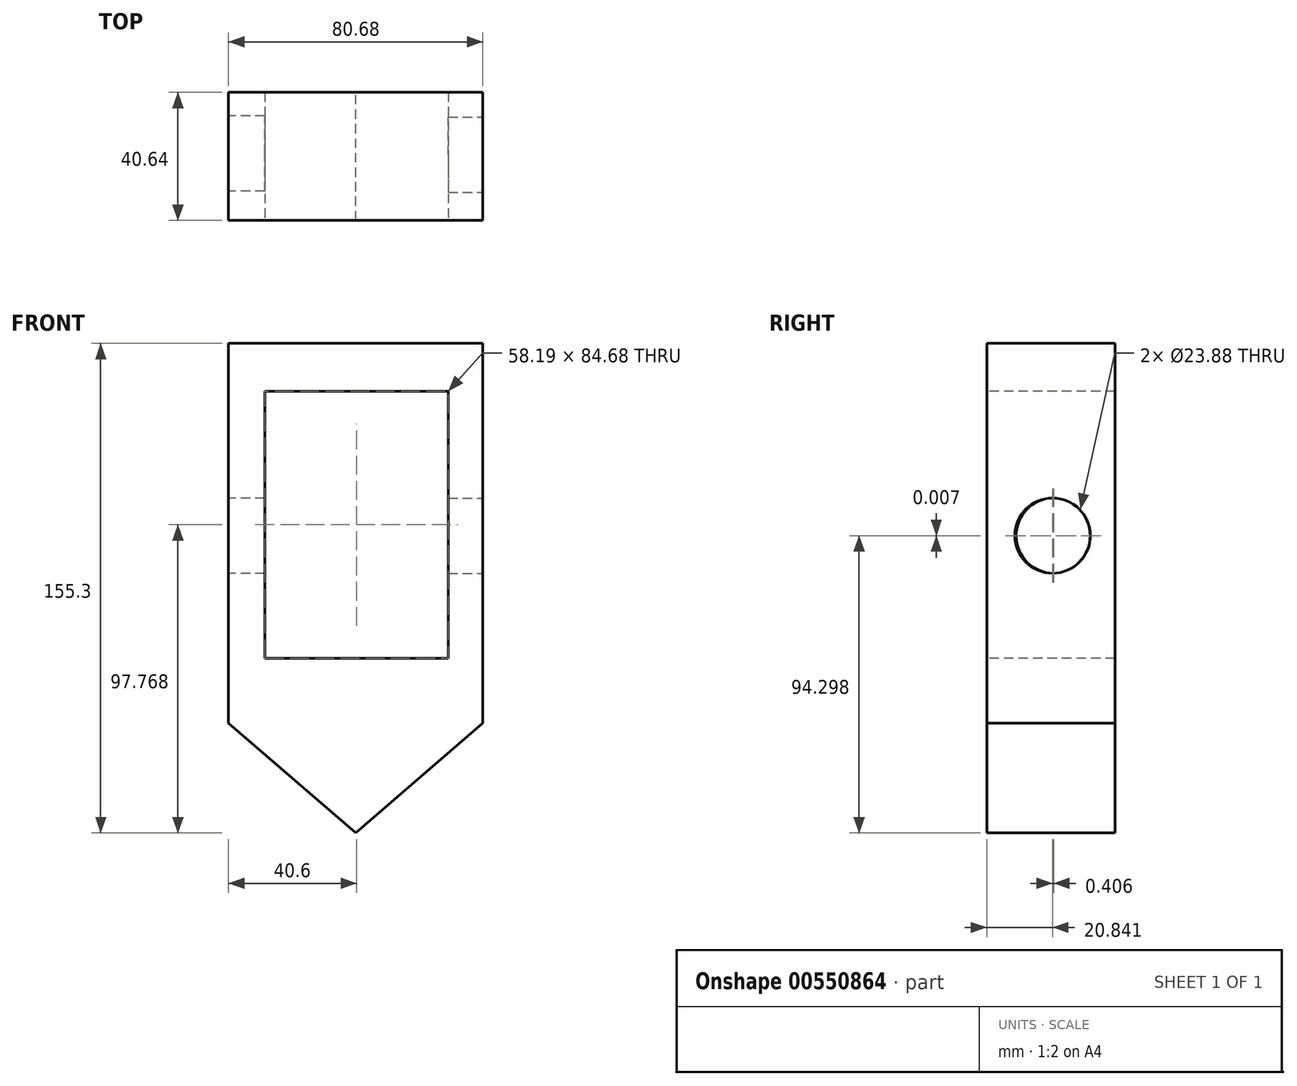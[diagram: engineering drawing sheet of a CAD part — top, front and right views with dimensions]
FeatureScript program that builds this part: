
annotation { "Feature Type Name" : "Feature", "Feature Type Description" : "" }
export const myFeature = defineFeature(function(context is Context, id is Id, definition is map)
    precondition{}
    {
        {
            var Q0;
            Q0=qCreatedBy(makeId("Front.planeOp"),FACE);
            var sketch = newSketch(context, id + "F0", { "sketchPlane" : qUnion([Q0])});
            skLineSegment(sketch, "E0", {"start": v(45.4, -28.3) * mm, "end": v(5.04, -63.13) * mm});
            skLineSegment(sketch, "E1", {"start": v(-35.29, -28.3) * mm, "end": v(5.04, -63.13) * mm});
            skLineSegment(sketch, "E2", {"start": v(-35.29, 92.17) * mm, "end": v(45.4, 92.17) * mm});
            skLineSegment(sketch, "E3", {"start": v(45.4, 92.17) * mm, "end": v(45.4, -28.3) * mm});
            skLineSegment(sketch, "E4", {"start": v(-35.29, 92.17) * mm, "end": v(-35.29, -28.3) * mm});
            skSolve(sketch);
        }
        {
            var Q0;
            Q0 = qSketchRegion(id + "F0", true);
            var Q1;
            Q1 = qSketchRegion(id + "F2", true);
            extrude(context, id + "F1", {"entities" : qUnion([Q0, Q1]), "depth" : 40.64 * mm, "offsetDistance" : 25.4 * mm});
        }
        {
            var Q0;
            Q0=makeQuery(id+"F1.opExtrude","CAP_FACE",FACE,{"disambiguationData":[OSD([sQuery(id+"F0.wireOp",EDGE,"E0"),sQuery(id+"F0.wireOp",EDGE,"E1"),sQuery(id+"F0.wireOp",EDGE,"E2"),sQuery(id+"F0.wireOp",EDGE,"E3"),sQuery(id+"F0.wireOp",EDGE,"E4")])],"isStart":false});
            var sketch = newSketch(context, id + "F2", { "sketchPlane" : qUnion([Q0])});
            skPoint(sketch, "E5.end.orphan", {"position": v(-13.85, 74.17) * mm});
            skPoint(sketch, "E5.start.orphan", {"position": v(34.4, 74.17) * mm});
            skPoint(sketch, "E6.end.orphan", {"position": v(34.4, -2.03) * mm});
            skLineSegment(sketch, "E7.bottom", {"start": v(-23.79, 76.98) * mm, "end": v(34.4, 76.98) * mm});
            skLineSegment(sketch, "E7.top", {"start": v(-23.79, -7.7) * mm, "end": v(34.4, -7.7) * mm});
            skLineSegment(sketch, "E7.left", {"start": v(-23.79, 76.98) * mm, "end": v(-23.79, -7.7) * mm});
            skLineSegment(sketch, "E7.right", {"start": v(34.4, 76.98) * mm, "end": v(34.4, -7.7) * mm});
            skSolve(sketch);
        }
        {
            var Q0;
            Q0=makeQuery(id+"F2.imprint","IMPRINT",FACE,{"disambiguationData":[TD([[makeQuery(id+"F2.imprint","IMPRINT",EDGE,{"derivedFrom":sQuery(id+"F2.wireOp",EDGE,"E7.bottom")}),-1.0]])]});
            extrude(context, id + "F3", {"entities" : qUnion([Q0]), "operationType" : NewBodyOperationType.REMOVE, "oppositeDirection" : true, "depth" : 100.58 * mm, "offsetDistance" : 25.4 * mm});
        }
        {
            var Q0;
            Q0 = qSketchRegion(id + "F2", true);
            extrude(context, id + "F4", {"entities" : qUnion([Q0]), "operationType" : NewBodyOperationType.REMOVE, "oppositeDirection" : true, "depth" : 25.4 * mm, "offsetDistance" : 25.4 * mm});
        }
        {
            var Q0;
            Q0=makeQuery(id+"F1.opExtrude","SWEPT_FACE",FACE,{"disambiguationData":[OSD([sQuery(id+"F0.wireOp",EDGE,"E4")])]});
            var sketch = newSketch(context, id + "F5", { "sketchPlane" : qUnion([Q0])});
            skCircle(sketch, "E8", {"center": v(19.4, 31.18) * mm, "radius": 11.94 * mm});
            skPoint(sketch, "E9.center.orphan", {"position": v(123.28, 92.17) * mm});
            skSolve(sketch);
        }
        {
            var Q0;
            Q0 = qSketchRegion(id + "F5", true);
            extrude(context, id + "F6", {"entities" : qUnion([Q0]), "operationType" : NewBodyOperationType.REMOVE, "oppositeDirection" : true, "depth" : 25.4 * mm, "offsetDistance" : 25.4 * mm});
        }
        {
            var Q0;
            Q0=makeQuery(id+"F1.opExtrude","SWEPT_FACE",FACE,{"disambiguationData":[OSD([sQuery(id+"F0.wireOp",EDGE,"E3")])]});
            var sketch = newSketch(context, id + "F7", { "sketchPlane" : qUnion([Q0])});
            skCircle(sketch, "E10", {"center": v(-19.8, 31.17) * mm, "radius": 11.94 * mm});
            skSolve(sketch);
        }
        {
            var Q0;
            Q0 = qSketchRegion(id + "F7", true);
            extrude(context, id + "F8", {"entities" : qUnion([Q0]), "operationType" : NewBodyOperationType.REMOVE, "oppositeDirection" : true, "depth" : 25.4 * mm, "offsetDistance" : 25.4 * mm});
        }
    });
